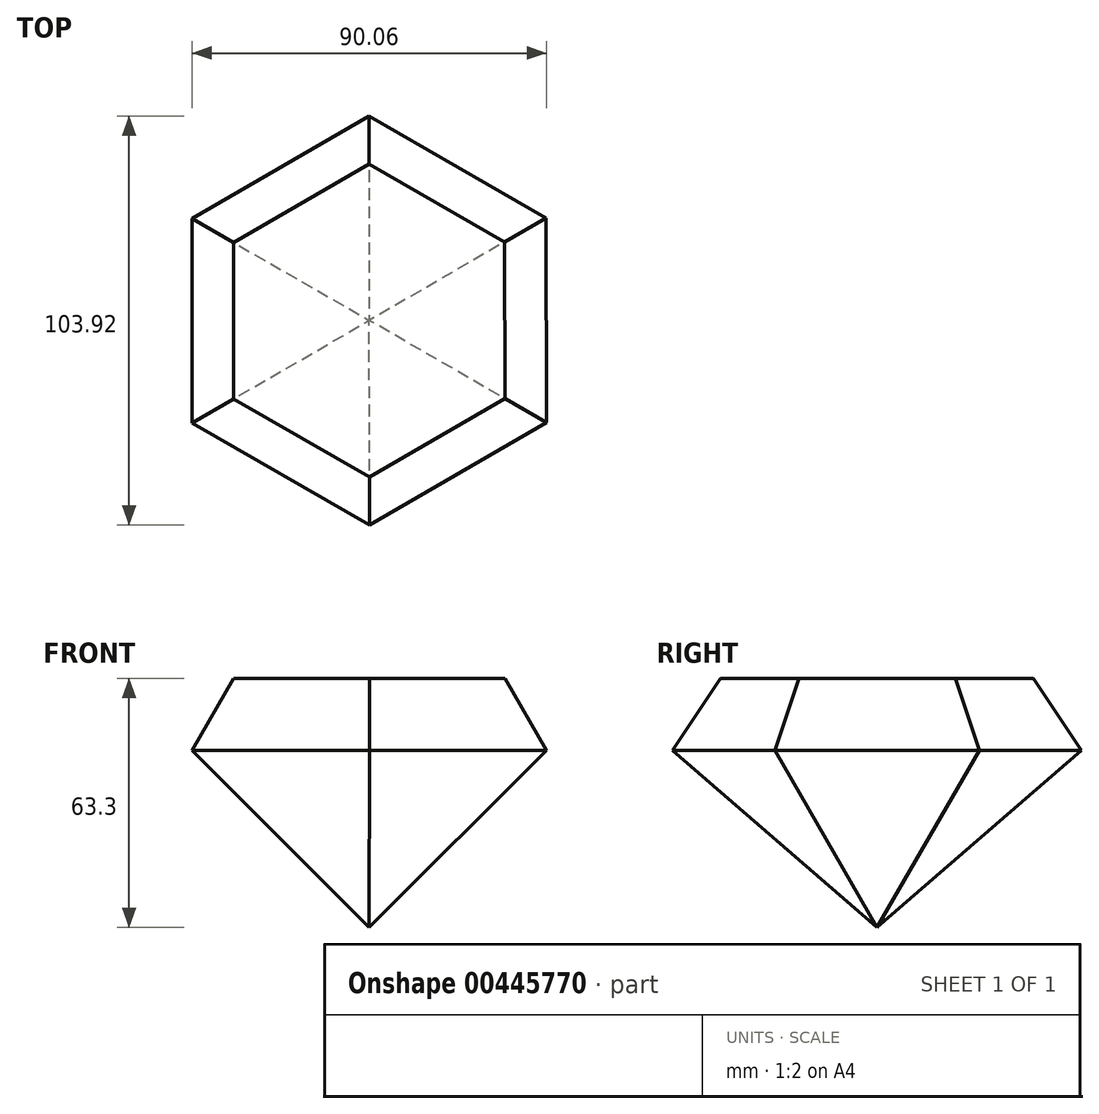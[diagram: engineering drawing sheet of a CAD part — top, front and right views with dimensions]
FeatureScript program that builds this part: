
annotation { "Feature Type Name" : "Feature", "Feature Type Description" : "" }
export const myFeature = defineFeature(function(context is Context, id is Id, definition is map)
    precondition{}
    {
        {
            var Q0;
            Q0=qCreatedBy(makeId("Top.planeOp"),FACE);
            var sketch = newSketch(context, id + "F0", { "sketchPlane" : qUnion([Q0])});
            skCircle(sketch, "E0.cCircle", {"center": v(0, 0) * mm, "radius": 45 * mm, "construction": true});
            skLineSegment(sketch, "E0.0", {"start": v(45.03, -25.92) * mm, "end": v(0.07, -51.96) * mm});
            skLineSegment(sketch, "E0.1", {"start": v(0.07, -51.96) * mm, "end": v(-44.97, -26.04) * mm});
            skLineSegment(sketch, "E0.2", {"start": v(-44.97, -26.04) * mm, "end": v(-45.03, 25.92) * mm});
            skLineSegment(sketch, "E0.3", {"start": v(-45.03, 25.92) * mm, "end": v(-0.07, 51.96) * mm});
            skLineSegment(sketch, "E0.4", {"start": v(-0.07, 51.96) * mm, "end": v(44.97, 26.04) * mm});
            skLineSegment(sketch, "E0.5", {"start": v(44.97, 26.04) * mm, "end": v(45.03, -25.92) * mm});
            skPoint(sketch, "E0.0.midPoint", {"position": v(22.55, -38.94) * mm});
            skSolve(sketch);
        }
        {
            var Q0;
            Q0=makeQuery(id+"F0.imprint","IMPRINT",FACE,{"disambiguationData":[TD([[makeQuery(id+"F0.imprint","IMPRINT",EDGE,{"derivedFrom":sQuery(id+"F0.wireOp",EDGE,"E0.0")}),-1.0]])]});
            extrude(context, id + "F1", {"entities" : qUnion([Q0]), "depth" : 18.3 * mm, "hasDraft" : true, "draftAngle" : 30 * degree, "draftPullDirection" : true, "hasSecondDirection" : true, "secondDirectionOppositeDirection" : true, "secondDirectionDepth" : 53.2 * mm, "hasSecondDirectionDraft" : true, "secondDirectionDraftAngle" : 45 * degree, "secondDirectionDraftPullDirection" : true});
        }
    });
